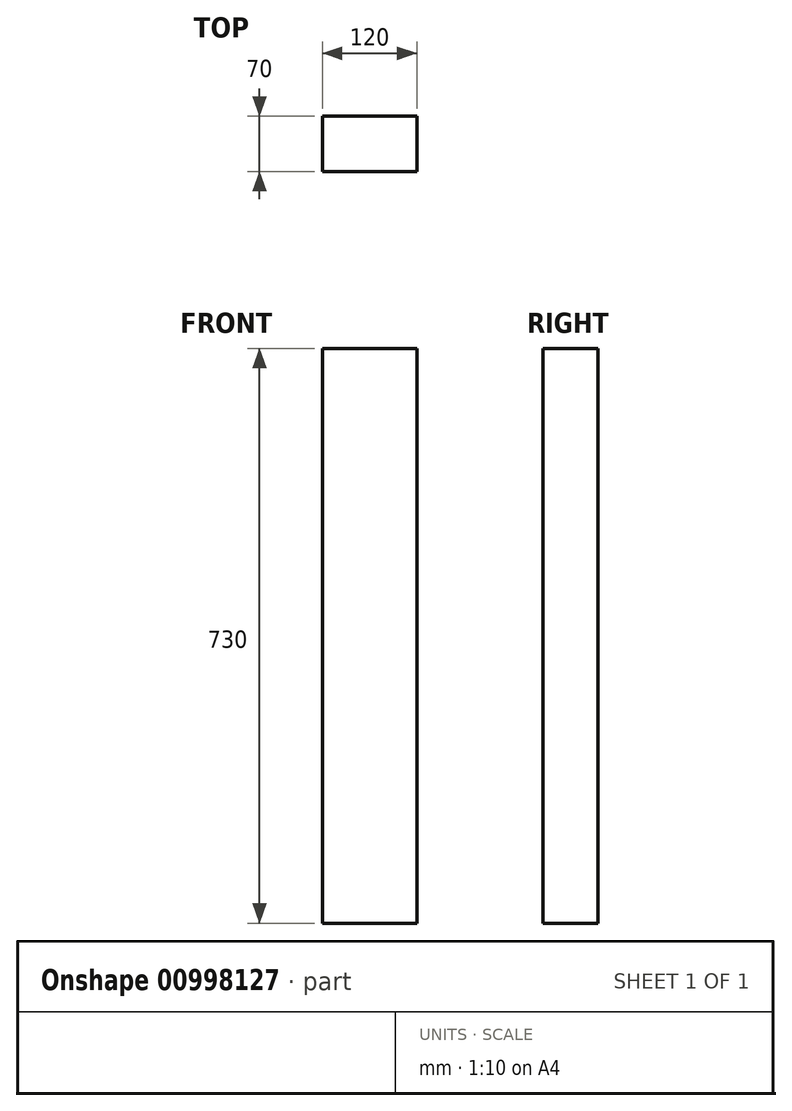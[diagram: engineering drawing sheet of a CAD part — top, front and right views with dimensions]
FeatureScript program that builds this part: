
annotation { "Feature Type Name" : "Feature", "Feature Type Description" : "" }
export const myFeature = defineFeature(function(context is Context, id is Id, definition is map)
    precondition{}
    {
        {
            var Q0;
            Q0=qCreatedBy(makeId("Front.planeOp"),FACE);
            var sketch = newSketch(context, id + "F0", { "sketchPlane" : qUnion([Q0])});
            skLineSegment(sketch, "E0.bottom", {"start": v(0, 0) * mm, "end": v(120, 0) * mm});
            skLineSegment(sketch, "E0.top", {"start": v(0, 730) * mm, "end": v(120, 730) * mm});
            skLineSegment(sketch, "E0.left", {"start": v(0, 0) * mm, "end": v(0, 730) * mm});
            skLineSegment(sketch, "E0.right", {"start": v(120, 0) * mm, "end": v(120, 730) * mm});
            skSolve(sketch);
        }
        {
            var Q0;
            Q0 = qSketchRegion(id + "F0", true);
            extrude(context, id + "F1", {"entities" : qUnion([Q0]), "depth" : 70 * mm, "offsetDistance" : 25 * mm});
        }
        {
            var Q0;
            Q0=makeQuery(id+"F1.opExtrude","CAP_FACE",FACE,{"disambiguationData":[OSD([sQuery(id+"F0.wireOp",EDGE,"E0.bottom"),sQuery(id+"F0.wireOp",EDGE,"E0.top"),sQuery(id+"F0.wireOp",EDGE,"E0.left"),sQuery(id+"F0.wireOp",EDGE,"E0.right")])],"isStart":false});
            var sketch = newSketch(context, id + "F2", { "sketchPlane" : qUnion([Q0])});
            skLineSegment(sketch, "E1.bottom", {"start": v(-60, -365) * mm, "end": v(60, -365) * mm});
            skLineSegment(sketch, "E1.top", {"start": v(-60, 365) * mm, "end": v(60, 365) * mm});
            skLineSegment(sketch, "E1.left", {"start": v(-60, -365) * mm, "end": v(-60, 365) * mm});
            skLineSegment(sketch, "E1.right", {"start": v(60, -365) * mm, "end": v(60, 365) * mm});
            skSolve(sketch);
        }
        {
            var Q0;
            Q0=makeQuery(id+"F1.opExtrude","SWEPT_BODY",BODY,{"disambiguationData":[OSD([sQuery(id+"F0.wireOp",EDGE,"E0.bottom"),sQuery(id+"F0.wireOp",EDGE,"E0.top"),sQuery(id+"F0.wireOp",EDGE,"E0.left"),sQuery(id+"F0.wireOp",EDGE,"E0.right")])]});
            var Q1;
            Q1=sQuery(id+"F2.wireOp",EDGE,"E1.left");
            transform(context, id + "F3", {"entities" : qUnion([Q0]), "transformType" : TransformType.TRANSLATION_ENTITY, "oppositeDirectionEntity" : false, "transformLine" : qUnion([Q1]), "makeCopy" : false});
        }
        {
            var Q0;
            Q0=makeQuery(id+"F1.opExtrude","SWEPT_BODY",BODY,{"disambiguationData":[OSD([sQuery(id+"F0.wireOp",EDGE,"E0.bottom"),sQuery(id+"F0.wireOp",EDGE,"E0.top"),sQuery(id+"F0.wireOp",EDGE,"E0.left"),sQuery(id+"F0.wireOp",EDGE,"E0.right")])]});
            var Q1;
            Q1=qCreatedBy(makeId("Front.planeOp"),FACE);
            var Q2;
            Q2=qCreatedBy(id+"FluNSHGhyOdgzoa_1.mateConnectorOp",VERTEX);
            transform(context, id + "F4", {"entities" : qUnion([Q0]), "transformType" : TransformType.TRANSLATION_DISTANCE, "transformDirection" : qUnion([Q1]), "distance" : 25 * mm, "makeCopy" : false});
        }
    });
